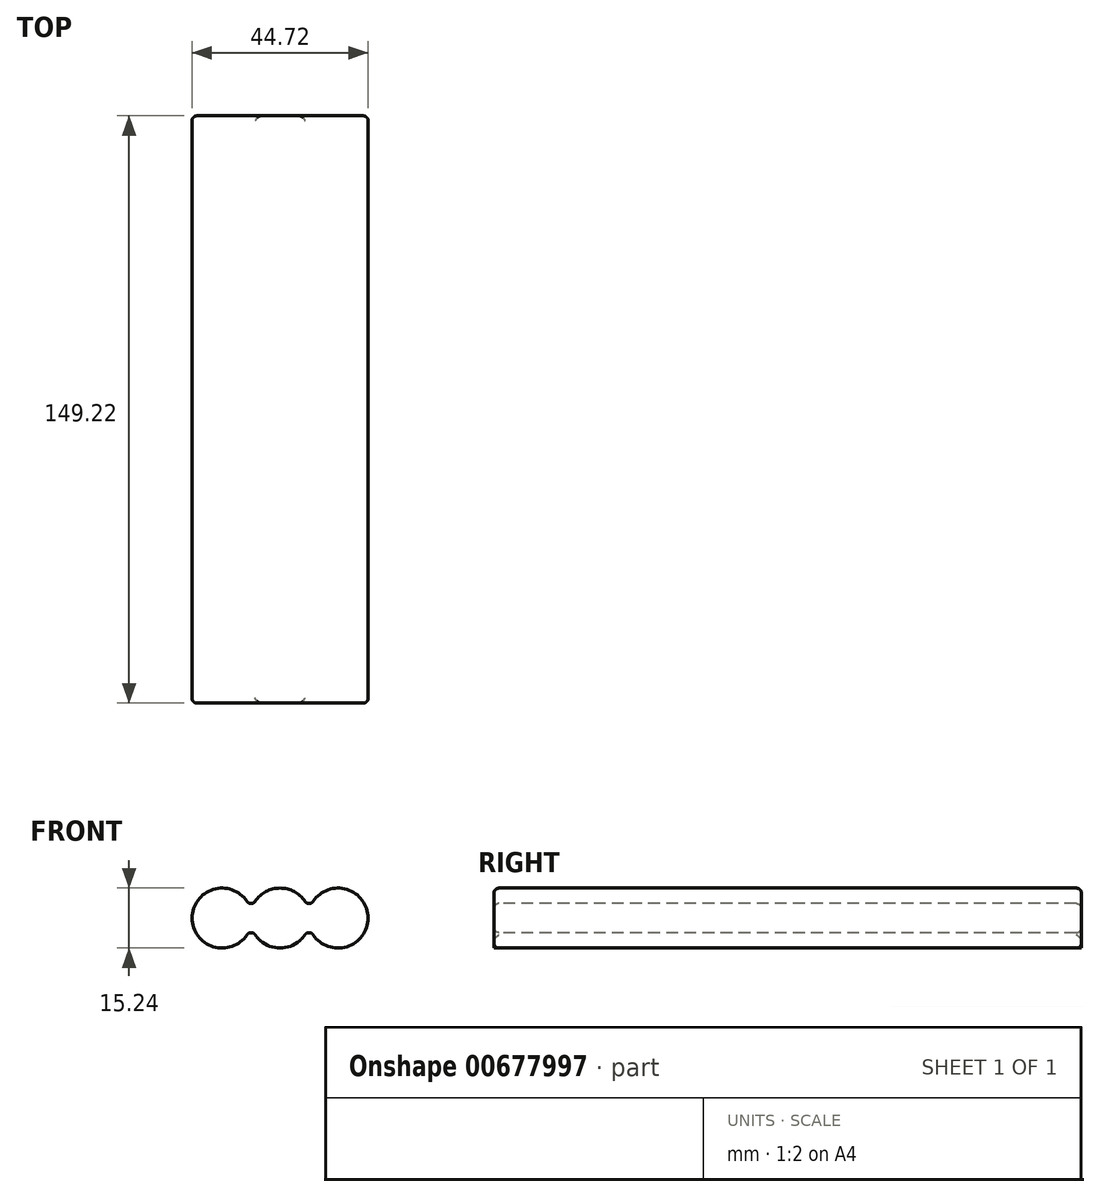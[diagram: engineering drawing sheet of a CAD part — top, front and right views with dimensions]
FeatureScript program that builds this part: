
annotation { "Feature Type Name" : "Feature", "Feature Type Description" : "" }
export const myFeature = defineFeature(function(context is Context, id is Id, definition is map)
    precondition{}
    {
        {
            var Q0;
            Q0=qCreatedBy(makeId("Front.planeOp"),FACE);
            var sketch = newSketch(context, id + "F0", { "sketchPlane" : qUnion([Q0])});
            skArc(sketch, "E0", {"start": v(-7.37, -1.93) * mm, "mid": v(0, -7.62) * mm, "end": v(7.37, -1.93) * mm});
            skArc(sketch, "E1", {"start": v(-7.37, 1.93) * mm, "mid": v(-22.36, 0) * mm, "end": v(-7.37, -1.93) * mm});
            skArc(sketch, "E2", {"start": v(7.37, -1.93) * mm, "mid": v(22.36, 0) * mm, "end": v(7.37, 1.93) * mm});
            skPoint(sketch, "E2.centerSnap0", {"position": v(7.62, 0) * mm});
            skArc(sketch, "E3.trimOffspring", {"start": v(7.37, 1.93) * mm, "mid": v(0, 7.62) * mm, "end": v(-7.37, 1.93) * mm});
            skLineSegment(sketch, "E4", {"start": v(-14.74, 0) * mm, "end": v(0, 0) * mm, "construction": true});
            skLineSegment(sketch, "E5", {"start": v(0, 0) * mm, "end": v(14.74, 0) * mm, "construction": true});
            skLineSegment(sketch, "E6", {"start": v(-7.37, 1.93) * mm, "end": v(7.37, 1.93) * mm, "construction": true});
            skLineSegment(sketch, "E7", {"start": v(7.37, -1.93) * mm, "end": v(-7.37, -1.93) * mm, "construction": true});
            skSolve(sketch);
        }
        {
            var Q0;
            Q0=makeQuery(id+"F0.imprint","IMPRINT",FACE,{"disambiguationData":[TD([[makeQuery(id+"F0.imprint","IMPRINT",EDGE,{"derivedFrom":sQuery(id+"F0.wireOp",EDGE,"E0")}),1.0]])]});
            extrude(context, id + "F1", {"entities" : qUnion([Q0]), "depth" : 149.22 * mm, "offsetDistance" : 25.4 * mm, "symmetric" : true});
        }
        {
            var Q0;
            Q0=makeQuery(id+"F1.opExtrude","SWEPT_FACE",FACE,{"disambiguationData":[OSD([sQuery(id+"F0.wireOp",EDGE,"E3.trimOffspring")])]});
            var Q1;
            Q1=makeQuery(id+"F1.opExtrude","SWEPT_FACE",FACE,{"disambiguationData":[OSD([sQuery(id+"F0.wireOp",EDGE,"E2")])]});
            var Q2;
            Q2=makeQuery(id+"F1.opExtrude","SWEPT_FACE",FACE,{"disambiguationData":[OSD([sQuery(id+"F0.wireOp",EDGE,"E1")])]});
            fillet(context, id + "F2", {"entities" : qUnion([Q0, Q1, Q2]), "radius" : 1.27 * mm, "tangentPropagation" : true, "allowEdgeOverflow" : false});
        }
    });
